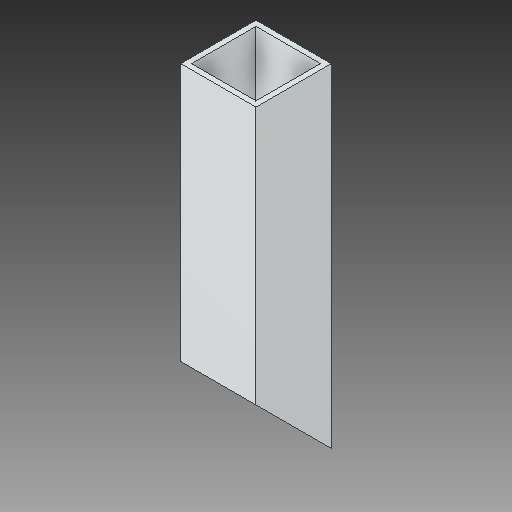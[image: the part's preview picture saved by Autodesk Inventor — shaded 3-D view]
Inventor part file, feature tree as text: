
AUTODESK INVENTOR PART (.ipt)
format: ipt  version: 2018 (Build 220112000, 112)  size: 87,040 bytes
history: native  units: in
note: dims shown in document units (in); Inventor stores cm internally (conversion verified against a paired STEP export)
features: chamfer x1
ambient origin geometry x8: Origin, YZ Plane, XZ Plane, XY Plane, X Axis, Y Axis, Z Axis, Center Point
bodies: Solid1 (feature_tree)
feature tree (1):
  chamfer  "Chamfer1"  [1 undecoded]
note: 1 required parameter value undecoded (feature->parameter linkage not recoverable at this tier; creation-order binding heuristic only, values carry confidence <= 0.55)
